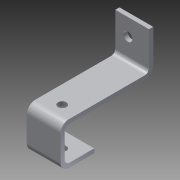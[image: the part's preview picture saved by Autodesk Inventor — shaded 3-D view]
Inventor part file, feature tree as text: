
AUTODESK INVENTOR PART (.ipt)
format: ipt  version: 2013 (Build 170138000, 138)  size: 215,040 bytes
history: native  units: in
note: dims shown in document units (in); Inventor stores cm internally (conversion verified against a paired STEP export)
features: sheet_metal_op x10, other x6, sketch x5, extrude x1, reference x1
ambient origin geometry x8: Origin, YZ Plane, XZ Plane, XY Plane, X Axis, Y Axis, Z Axis, Center Point
bodies: Solid1 (feature_tree)
feature tree (23):
  sheet_metal_op  "Face1"
  sheet_metal_op  "Flange1"
  sheet_metal_op  "Flange2"
  sheet_metal_op  "Flange3"
  extrude  "Extrusion1"  Depth=0.125in
  sketch  "Sketch1"  dims[d0=0.125in d1=0.125in]
  other  "Plate1"
  sketch  "Sketch2"  dims[d2=0.0625in]
  other  "Plate2"
  sheet_metal_op  "Bend1"
  sheet_metal_op  "Corner1"
  sketch  "Sketch3"  dims[d3=0.25in]
  other  "Plate3"
  sheet_metal_op  "Bend2"
  sheet_metal_op  "Corner2"
  sketch  "Sketch4"  dims[d4=0.125in]
  other  "Plate4"
  sheet_metal_op  "Bend3"
  sheet_metal_op  "Corner3"
  sketch  "Sketch5"  dims[d5=2.5in d6=90.0deg d7=0.125in d8=0.5in d9=0.125in d10=0.125in d11=0.125in d12=0.0625in d13=0.25in d14=0.125in d15=1.0in d16=90.0deg d17=0.125in d18=0.5in d19=0.125in d20=0.125in d21=0.125in d22=0.0625in d23=0.25in d24=0.125in d25=1.0in d26=90.0deg d27=0.125in d28=0.5in d29=0.125in d30=0.125in d31=2.1in d33=1.2784in d34=0.25in d35=1.5in d36=0.0in d37=1.0in d38=0.375in]
  reference  "Reference1"
  other  "Definition1"
  other  "Cut1"
